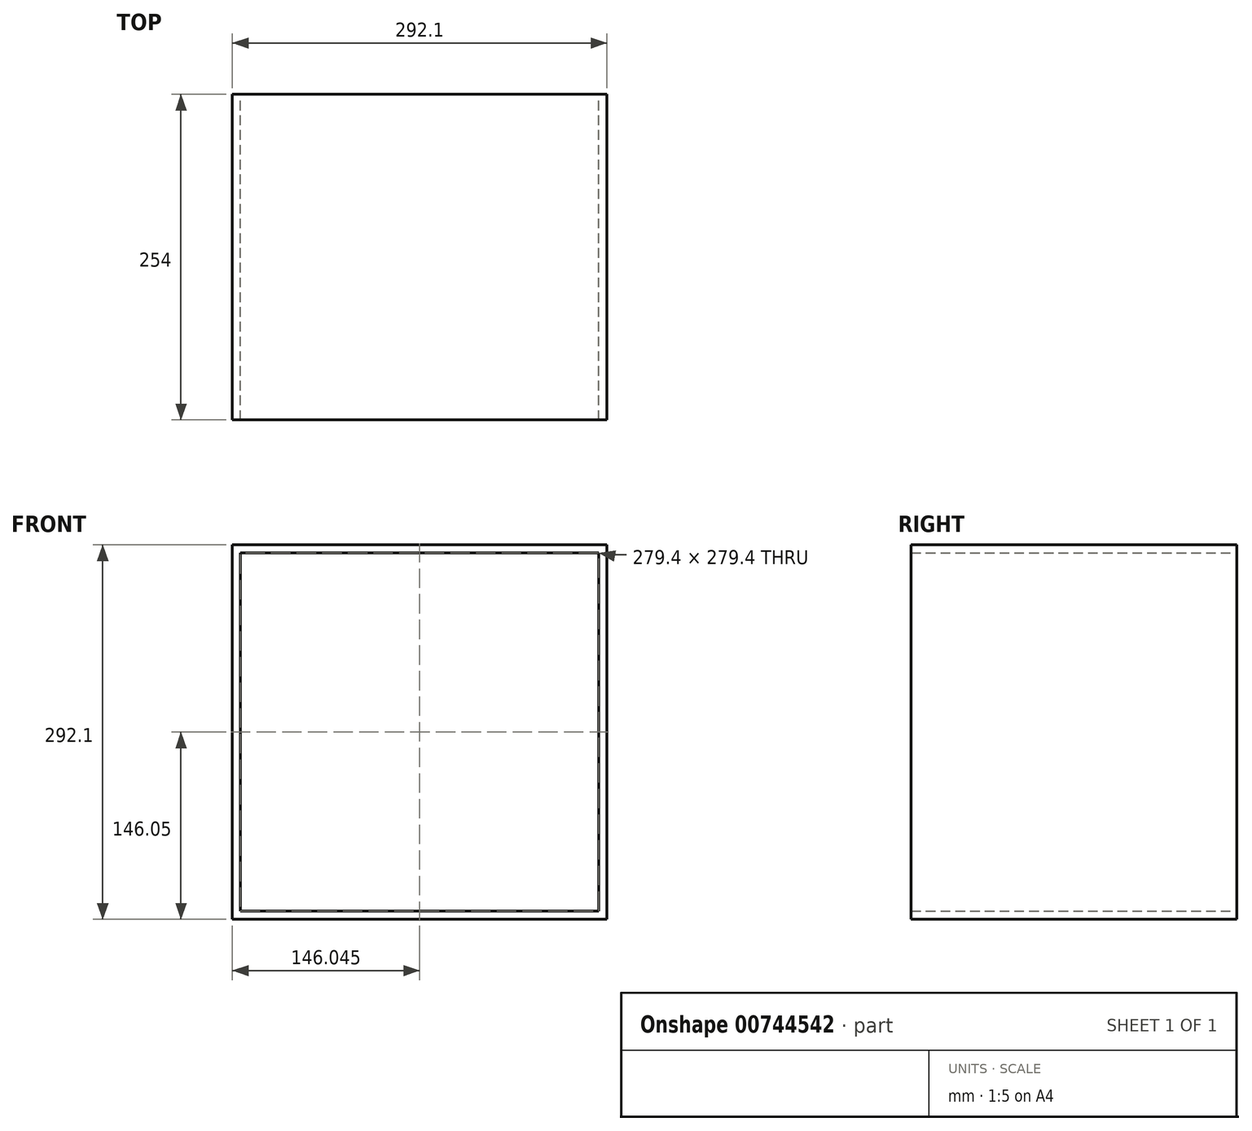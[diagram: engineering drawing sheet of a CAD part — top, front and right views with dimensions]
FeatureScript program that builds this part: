
annotation { "Feature Type Name" : "Feature", "Feature Type Description" : "" }
export const myFeature = defineFeature(function(context is Context, id is Id, definition is map)
    precondition{}
    {
        {
            var Q0;
            Q0=qCreatedBy(makeId("Front.planeOp"),FACE);
            var sketch = newSketch(context, id + "F0", { "sketchPlane" : qUnion([Q0])});
            skLineSegment(sketch, "E0.bottom", {"start": v(9.25, 0) * mm, "end": v(301.35, 0) * mm});
            skLineSegment(sketch, "E0.top", {"start": v(9.25, 292.1) * mm, "end": v(301.35, 292.1) * mm});
            skLineSegment(sketch, "E0.left", {"start": v(9.25, 0) * mm, "end": v(9.25, 292.1) * mm});
            skLineSegment(sketch, "E0.right", {"start": v(301.35, 0) * mm, "end": v(301.35, 292.1) * mm});
            skLineSegment(sketch, "E1.0", {"start": v(295, 6.35) * mm, "end": v(295, 285.75) * mm});
            skLineSegment(sketch, "E1.1", {"start": v(15.6, 6.35) * mm, "end": v(295, 6.35) * mm});
            skLineSegment(sketch, "E1.2", {"start": v(15.6, 6.35) * mm, "end": v(15.6, 285.75) * mm});
            skLineSegment(sketch, "E1.3", {"start": v(15.6, 285.75) * mm, "end": v(295, 285.75) * mm});
            skSolve(sketch);
        }
        {
            var Q0;
            Q0 = qSketchRegion(id + "F0", true);
            extrude(context, id + "F1", {"entities" : qUnion([Q0]), "depth" : 254 * mm, "offsetDistance" : 25.4 * mm});
        }
    });
